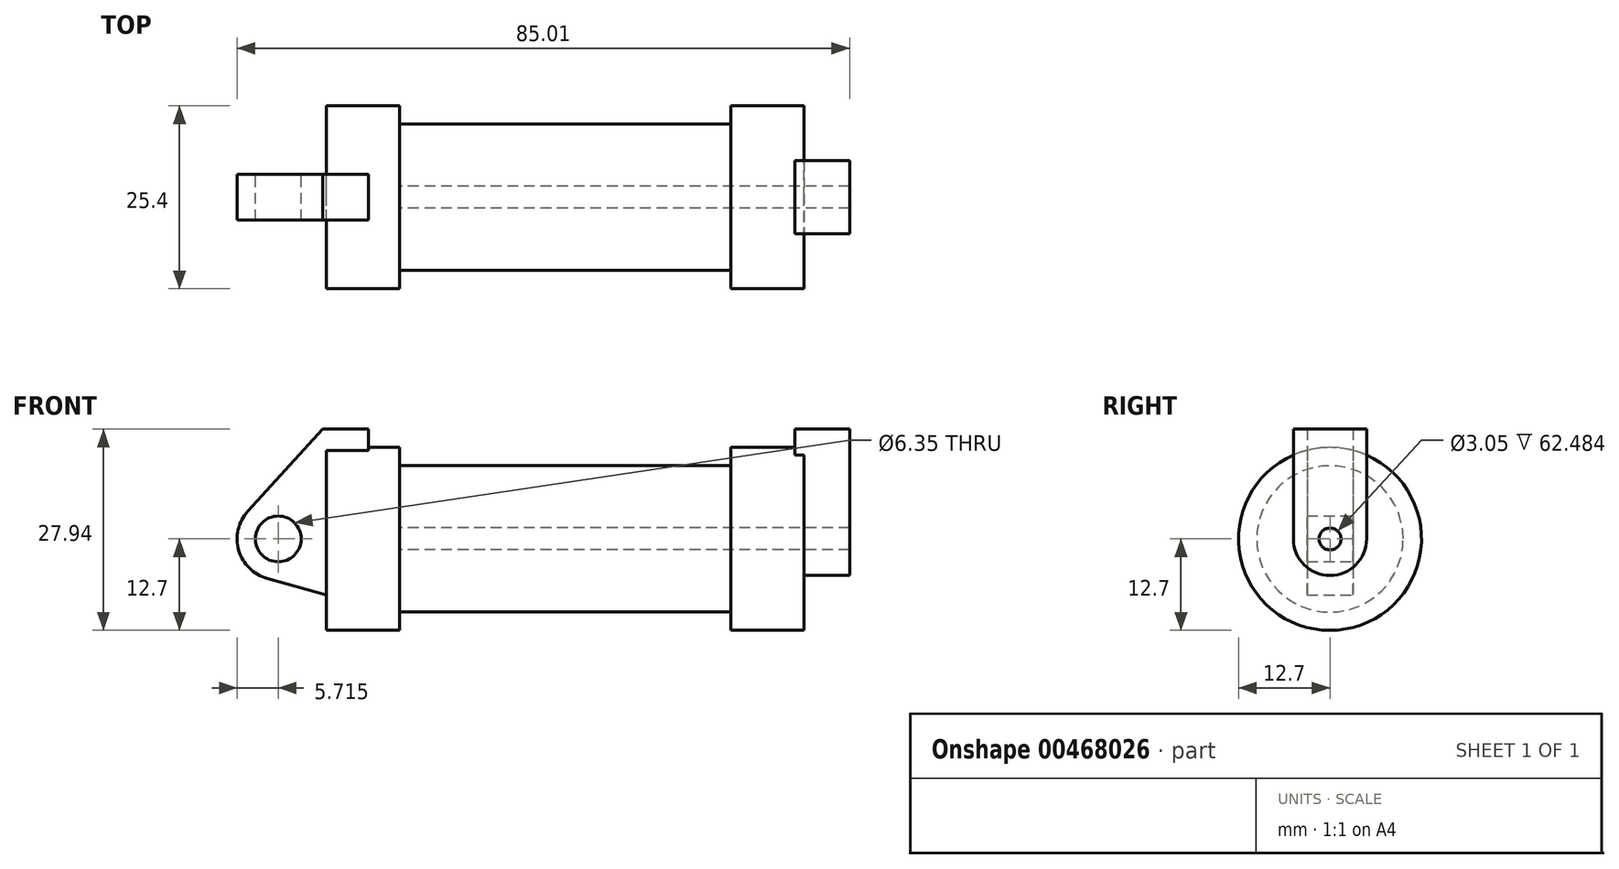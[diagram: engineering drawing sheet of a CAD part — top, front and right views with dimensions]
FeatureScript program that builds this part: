
annotation { "Feature Type Name" : "Feature", "Feature Type Description" : "" }
export const myFeature = defineFeature(function(context is Context, id is Id, definition is map)
    precondition{}
    {
        {
            var Q0;
            Q0=qCreatedBy(makeId("Front.planeOp"),FACE);
            var sketch = newSketch(context, id + "F0", { "sketchPlane" : qUnion([Q0])});
            skLineSegment(sketch, "E0", {"start": v(0, 0) * mm, "end": v(0, 12.7) * mm});
            skLineSegment(sketch, "E1", {"start": v(0, 12.7) * mm, "end": v(10.16, 12.7) * mm});
            skLineSegment(sketch, "E2", {"start": v(10.16, 12.7) * mm, "end": v(10.16, 10.16) * mm});
            skLineSegment(sketch, "E3", {"start": v(10.16, 10.16) * mm, "end": v(56.13, 10.16) * mm});
            skLineSegment(sketch, "E4", {"start": v(56.13, 10.16) * mm, "end": v(56.13, 12.7) * mm});
            skLineSegment(sketch, "E5", {"start": v(56.13, 12.7) * mm, "end": v(66.3, 12.7) * mm});
            skLineSegment(sketch, "E6", {"start": v(66.3, 12.7) * mm, "end": v(66.3, 0) * mm});
            skLineSegment(sketch, "E7", {"start": v(66.3, 0) * mm, "end": v(0, 0) * mm});
            skLineSegment(sketch, "E8", {"start": v(5.84, 15.24) * mm, "end": v(-0.5, 15.24) * mm});
            skLineSegment(sketch, "E9", {"start": v(-0.5, 15.24) * mm, "end": v(-10.88, 3.85) * mm});
            skLineSegment(sketch, "E10", {"start": v(0, 0) * mm, "end": v(-6.65, 0) * mm});
            skCircle(sketch, "E11", {"center": v(-6.65, 0) * mm, "radius": 5.72 * mm});
            skCircle(sketch, "E12", {"center": v(-6.65, 0) * mm, "radius": 3.18 * mm});
            skLineSegment(sketch, "E13", {"start": v(5.84, 15.24) * mm, "end": v(5.84, -9.4) * mm});
            skLineSegment(sketch, "E14", {"start": v(5.84, -9.4) * mm, "end": v(-8.18, -5.5) * mm});
            skSolve(sketch);
        }
        {
            var Q0;
            {var subQ0=sQuery(id+"F0.wireOp",EDGE,"E2");Q0=makeQuery(id+"F0.imprint","IMPRINT",FACE,{"disambiguationData":[TD([[makeQuery(id+"F0.imprint","IMPRINT",EDGE,{"derivedFrom":subQ0}),-1.0]])]});}
            var Q1;
            {var subQ0=sQuery(id+"F0.wireOp",EDGE,"E0");Q1=makeQuery(id+"F0.imprint","IMPRINT",FACE,{"disambiguationData":[TD([[makeQuery(id+"F0.imprint","IMPRINT",EDGE,{"derivedFrom":subQ0}),-1.0]])]});}
            var Q2;
            Q2=sQuery(id+"F0.wireOp",EDGE,"E7");
            revolve(context, id + "F1", {"entities" : qUnion([Q0, Q1]), "axis" : qUnion([Q2]), "revolveType" : RevolveType.FULL});
        }
        {
            var Q0;
            Q0=makeQuery(id+"F1.opRevolve","SWEPT_FACE",FACE,{"disambiguationData":[OSD([sQuery(id+"F0.wireOp",EDGE,"E6")])]});
            var sketch = newSketch(context, id + "F2", { "sketchPlane" : qUnion([Q0])});
            skCircle(sketch, "E15", {"center": v(0, 0) * mm, "radius": 1.52 * mm});
            skCircle(sketch, "E16", {"center": v(0, 0) * mm, "radius": 5.08 * mm});
            skLineSegment(sketch, "E17", {"start": v(-5.08, 0) * mm, "end": v(-5.08, 15.24) * mm});
            skLineSegment(sketch, "E18", {"start": v(5.08, 0) * mm, "end": v(5.08, 15.24) * mm});
            skLineSegment(sketch, "E19", {"start": v(-5.08, 15.24) * mm, "end": v(5.08, 15.24) * mm});
            skSolve(sketch);
        }
        {
            var Q0;
            Q0 = qSketchRegion(id + "F2", true);
            extrude(context, id + "F3", {"entities" : qUnion([Q0]), "operationType" : NewBodyOperationType.ADD, "depth" : 6.35 * mm, "hasSecondDirection" : true, "secondDirectionOppositeDirection" : true, "secondDirectionDepth" : 1.27 * mm});
        }
        {
            var Q0;
            Q0=makeQuery(id+"F2.imprint","IMPRINT",FACE,{"disambiguationData":[TD([[makeQuery(id+"F2.imprint","IMPRINT",EDGE,{"derivedFrom":sQuery(id+"F2.wireOp",EDGE,"E15")}),1.0]])]});
            var Q1;
            Q1=makeQuery(id+"F1.opRevolve","SWEPT_FACE",FACE,{"disambiguationData":[OSD([sQuery(id+"F0.wireOp",EDGE,"E2")])]});
            extrude(context, id + "F4", {"entities" : qUnion([Q0]), "operationType" : NewBodyOperationType.REMOVE, "endBound" : BoundingType.UP_TO_SURFACE, "oppositeDirection" : true, "endBoundEntityFace" : qUnion([Q1]), "depth" : 25.4 * mm});
        }
        {
            var Q0;
            {var subQ1=sQuery(id+"F0.wireOp",EDGE,"E0");Q0=makeQuery(id+"F0.imprint","IMPRINT",FACE,{"disambiguationData":[TD([[makeQuery(id+"F0.imprint","IMPRINT",EDGE,{"derivedFrom":subQ1}),1.0]])]});}
            var Q1;
            {var subQ5=sQuery(id+"F0.wireOp",EDGE,"E12");Q1=makeQuery(id+"F0.imprint","IMPRINT",FACE,{"disambiguationData":[TD([[makeQuery(id+"F0.imprint","IMPRINT",EDGE,{"derivedFrom":subQ5}),-1.0]])]});}
            var Q2;
            {var subQ0=sQuery(id+"F0.wireOp",EDGE,"E14");Q2=makeQuery(id+"F0.imprint","IMPRINT",FACE,{"disambiguationData":[TD([[makeQuery(id+"F0.imprint","IMPRINT",EDGE,{"derivedFrom":subQ0}),-1.0]])]});}
            var Q3;
            {var subQ0=sQuery(id+"F0.wireOp",EDGE,"E0");Q3=makeQuery(id+"F0.imprint","IMPRINT",FACE,{"disambiguationData":[TD([[makeQuery(id+"F0.imprint","IMPRINT",EDGE,{"derivedFrom":subQ0}),-1.0]])]});}
            extrude(context, id + "F5", {"entities" : qUnion([Q0, Q1, Q2, Q3]), "operationType" : NewBodyOperationType.ADD, "depth" : 3.17 * mm, "hasSecondDirection" : true, "secondDirectionOppositeDirection" : true, "secondDirectionDepth" : 3.17 * mm});
        }
    });
